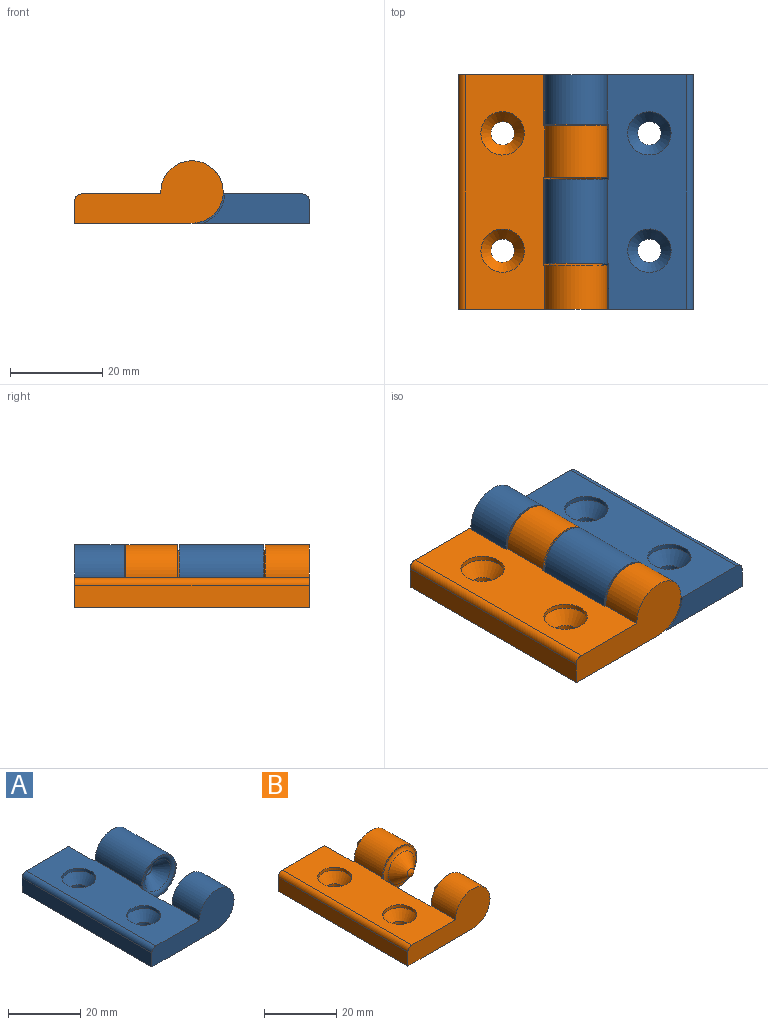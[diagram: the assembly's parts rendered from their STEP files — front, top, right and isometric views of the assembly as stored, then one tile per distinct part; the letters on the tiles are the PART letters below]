
ASSEMBLY  parts=2 mates=1
PART A: 28 faces, bbox 33.7x50.8x16.7 mm
  f0: cylinder r=6.75mm len=18.26mm, axis (0,-1,0), area 587.7mm2, adj f2,f3,f15,f18
  f1: plane 23.05x6.35mm, normal (0,1,0), area 124.1mm2, adj f2,f3,f4,f13,f17
  f2: plane 50.8x25.4mm, normal (0,0,-1), area 1198.5mm2, adj f0,f1,f4,f5,f6,f9,f12,f14
  f3: plane 50.8x17.08mm, normal (0,0,1), area 720.1mm2, adj f0,f1,f5,f6,f7,f10,f13,f14
  f4: plane 50.8x4.76mm, normal (-1,0,0), area 241.9mm2, adj f1,f2,f6,f13
  f5: cylinder r=6.75mm len=13.49mm, axis (0,-1,0), area 344.9mm2, adj f2,f3,f6,f16
  f6: plane 32.15x13.49mm, normal (0,-1,0), area 270.7mm2, adj f2,f3,f4,f5,f13
  f7: cylinder r=4.7mm len=9.4mm, axis (0,0,1), area 30mm2, adj f3,f8
  f8: cone r=4.7mm half-angle=35deg, axis (0,0,1), area 85.6mm2, adj f7,f9
  f9: cylinder r=2.54mm len=5.08mm, axis (0,0,1), area 35.9mm2, adj f2,f8
  f10: cylinder r=4.7mm len=9.4mm, axis (0,0,1), area 30mm2, adj f3,f11
  f11: cone r=4.7mm half-angle=35deg, axis (0,0,1), area 85.6mm2, adj f10,f12
  f12: cylinder r=2.54mm len=5.08mm, axis (0,0,1), area 35.9mm2, adj f2,f11
  f13: cylinder r=1.59mm len=50.8mm, axis (0,-1,0), area 126.7mm2, adj f1,f3,f4,f6
  f14: cylinder r=7.14mm len=11.91mm, axis (0,-1,0), area 100.4mm2, adj f2,f3,f15,f16
  f15: plane 13.88x13.49mm, normal (0,-1,0), area 19.9mm2, adj f0,f2,f3,f14,f27
  f16: plane 13.88x13.49mm, normal (0,1,0), area 19.9mm2, adj f2,f3,f5,f14,f22
  f17: cylinder r=7.14mm len=9.92mm, axis (0,1,0), area 83.7mm2, adj f1,f2,f3,f18
  f18: plane 13.88x13.49mm, normal (0,1,0), area 19.9mm2, adj f0,f2,f3,f17,f19
  f19: torus R=6.35mm, axis (0,-1,0), area 53.3mm2, adj f18,f20
  f20: cone r=4.99mm half-angle=45deg, axis (0,1,0), area 102.7mm2, adj f19,f21
  f21: sphere r=1.92mm, area 6.8mm2, adj f20
  f22: torus R=6.35mm, axis (0,-1,0), area 53.3mm2, adj f16,f23
  f23: cone r=4.99mm half-angle=45deg, axis (0,1,0), area 102.7mm2, adj f22,f24
  f24: sphere r=1.92mm, area 6.8mm2, adj f23
  f25: sphere r=1.92mm, area 6.8mm2, adj f26
  f26: cone r=4.99mm half-angle=45deg, axis (0,-1,0), area 102.7mm2, adj f25,f27
  f27: torus R=6.35mm, axis (0,-1,0), area 53.3mm2, adj f15,f26
PART B: 28 faces, bbox 33.7x50.8x16.7 mm
  f0: cylinder r=6.75mm len=13.49mm, axis (0,-1,0), area 357.7mm2, adj f2,f3,f15,f18
  f1: plane 23.05x6.35mm, normal (0,1,0), area 124.1mm2, adj f2,f3,f4,f13,f17
  f2: plane 50.8x25.4mm, normal (0,0,-1), area 1179mm2, adj f0,f1,f4,f5,f6,f9,f12,f14
  f3: plane 50.8x17.08mm, normal (0,0,1), area 716.8mm2, adj f0,f1,f5,f6,f7,f10,f13,f14
  f4: plane 50.8x4.76mm, normal (-1,0,0), area 241.9mm2, adj f1,f2,f6,f13
  f5: cylinder r=6.75mm len=13.49mm, axis (0,-1,0), area 306.6mm2, adj f2,f3,f6,f16
  f6: plane 32.15x13.49mm, normal (0,-1,0), area 270.7mm2, adj f2,f3,f4,f5,f13
  f7: cylinder r=4.7mm len=9.4mm, axis (0,0,1), area 30mm2, adj f3,f8
  f8: cone r=4.7mm half-angle=35deg, axis (0,0,1), area 85.6mm2, adj f7,f9
  f9: cylinder r=2.54mm len=5.08mm, axis (0,0,1), area 35.9mm2, adj f2,f8
  f10: cylinder r=4.7mm len=9.4mm, axis (0,0,1), area 30mm2, adj f3,f11
  f11: cone r=4.7mm half-angle=35deg, axis (0,0,1), area 85.6mm2, adj f10,f12
  f12: cylinder r=2.54mm len=5.08mm, axis (0,0,1), area 35.9mm2, adj f2,f11
  f13: cylinder r=1.59mm len=50.8mm, axis (0,-1,0), area 126.7mm2, adj f1,f3,f4,f6
  f14: cylinder r=7.14mm len=19.05mm, axis (0,-1,0), area 160.6mm2, adj f2,f3,f15,f16
  f15: plane 13.88x13.49mm, normal (0,-1,0), area 19.9mm2, adj f0,f2,f3,f14,f22
  f16: plane 13.88x13.49mm, normal (0,1,0), area 19.9mm2, adj f2,f3,f5,f14,f20
  f17: cylinder r=7.14mm len=11.11mm, axis (0,1,0), area 93.7mm2, adj f1,f2,f3,f18
  f18: plane 13.88x13.49mm, normal (0,1,0), area 19.9mm2, adj f0,f2,f3,f17,f25
  f19: cone r=4.99mm half-angle=45deg, axis (0,-1,0), area 102.7mm2, adj f20,f21
  f20: torus R=6.35mm, axis (0,-1,0), area 53.3mm2, adj f16,f19
  f21: sphere r=1.92mm, area 6.8mm2, adj f19
  f22: torus R=6.35mm, axis (0,-1,0), area 53.3mm2, adj f15,f23
  f23: cone r=4.99mm half-angle=45deg, axis (0,1,0), area 102.7mm2, adj f22,f24
  f24: sphere r=1.92mm, area 6.8mm2, adj f23
  f25: torus R=6.35mm, axis (0,-1,0), area 53.3mm2, adj f18,f27
  f26: sphere r=1.92mm, area 6.8mm2, adj f27
  f27: cone r=4.99mm half-angle=45deg, axis (0,-1,0), area 102.7mm2, adj f25,f26
PLACE A rot(axis=(0,0,1),180deg) t=(13.28,25.6,0)mm
PLACE B t=(13.28,-25.2,0)mm
MATE revolute A.f0 <-> B.f0  axis (0,-1,0) through (13.28,-15.28,6.75)mm
